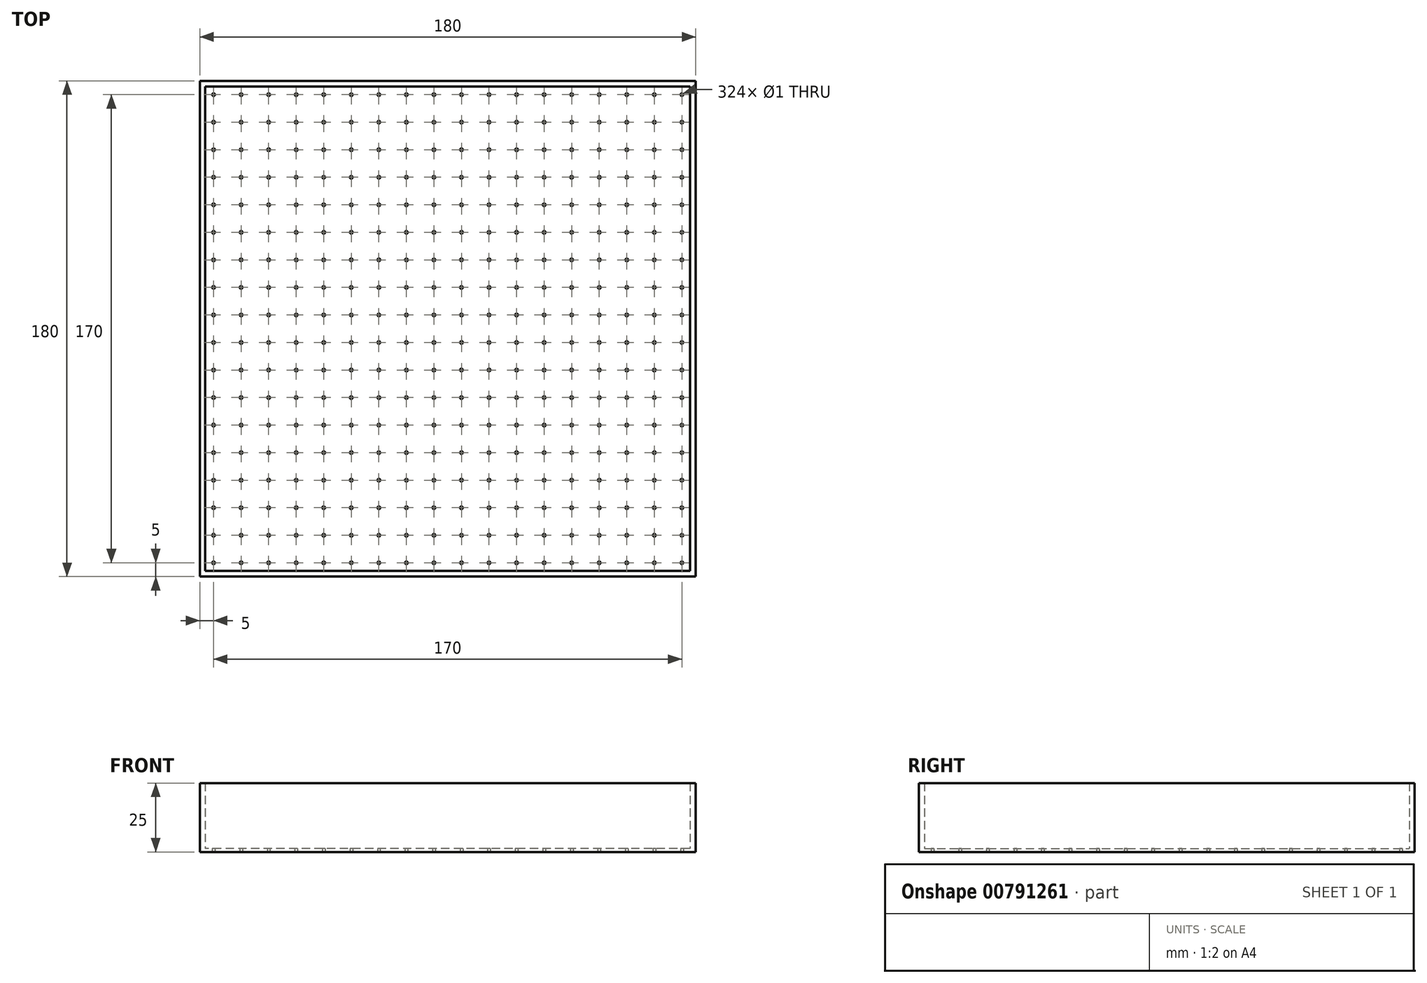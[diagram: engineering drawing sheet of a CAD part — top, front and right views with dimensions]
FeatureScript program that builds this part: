
annotation { "Feature Type Name" : "Feature", "Feature Type Description" : "" }
export const myFeature = defineFeature(function(context is Context, id is Id, definition is map)
    precondition{}
    {
        {
            var Q0;
            Q0=qCreatedBy(makeId("Top.planeOp"),FACE);
            var sketch = newSketch(context, id + "F0", { "sketchPlane" : qUnion([Q0])});
            skLineSegment(sketch, "E0.bottom", {"start": v(0, 0) * mm, "end": v(180, 0) * mm});
            skLineSegment(sketch, "E0.top", {"start": v(0, -180) * mm, "end": v(180, -180) * mm});
            skLineSegment(sketch, "E0.left", {"start": v(0, 0) * mm, "end": v(0, -180) * mm});
            skLineSegment(sketch, "E0.right", {"start": v(180, 0) * mm, "end": v(180, -180) * mm});
            skLineSegment(sketch, "E1.bottom", {"start": v(2, -2) * mm, "end": v(178, -2) * mm});
            skLineSegment(sketch, "E1.top", {"start": v(2, -178) * mm, "end": v(178, -178) * mm});
            skLineSegment(sketch, "E1.left", {"start": v(2, -2) * mm, "end": v(2, -178) * mm});
            skLineSegment(sketch, "E1.right", {"start": v(178, -2) * mm, "end": v(178, -178) * mm});
            skCircle(sketch, "E2", {"center": v(5, -5) * mm, "radius": 0.5 * mm});
            skCircle(sketch, "E3.1.0.0", {"center": v(15, -5) * mm, "radius": 0.5 * mm});
            skCircle(sketch, "E3.2.0.0", {"center": v(25, -5) * mm, "radius": 0.5 * mm});
            skLineSegment(sketch, "E3.direction1", {"start": v(5, -5) * mm, "end": v(15, -5) * mm, "construction": true});
            skCircle(sketch, "E4.0.3.0", {"center": v(35, -5) * mm, "radius": 0.5 * mm});
            skCircle(sketch, "E4.0.4.0", {"center": v(45, -5) * mm, "radius": 0.5 * mm});
            skCircle(sketch, "E4.0.5.0", {"center": v(55, -5) * mm, "radius": 0.5 * mm});
            skCircle(sketch, "E4.0.6.0", {"center": v(65, -5) * mm, "radius": 0.5 * mm});
            skCircle(sketch, "E4.0.7.0", {"center": v(75, -5) * mm, "radius": 0.5 * mm});
            skCircle(sketch, "E4.0.8.0", {"center": v(85, -5) * mm, "radius": 0.5 * mm});
            skCircle(sketch, "E4.0.9.0", {"center": v(95, -5) * mm, "radius": 0.5 * mm});
            skCircle(sketch, "E4.0.10.0", {"center": v(105, -5) * mm, "radius": 0.5 * mm});
            skCircle(sketch, "E4.0.11.0", {"center": v(115, -5) * mm, "radius": 0.5 * mm});
            skCircle(sketch, "E4.0.12.0", {"center": v(125, -5) * mm, "radius": 0.5 * mm});
            skCircle(sketch, "E4.0.13.0", {"center": v(135, -5) * mm, "radius": 0.5 * mm});
            skCircle(sketch, "E4.0.14.0", {"center": v(145, -5) * mm, "radius": 0.5 * mm});
            skCircle(sketch, "E4.0.15.0", {"center": v(155, -5) * mm, "radius": 0.5 * mm});
            skCircle(sketch, "E4.0.16.0", {"center": v(165, -5) * mm, "radius": 0.5 * mm});
            skCircle(sketch, "E4.0.17.0", {"center": v(175, -5) * mm, "radius": 0.5 * mm});
            skLineSegment(sketch, "E5.1.0.0", {"start": v(5, -15) * mm, "end": v(15, -15) * mm, "construction": true});
            skCircle(sketch, "E5.1.0.1", {"center": v(125, -15) * mm, "radius": 0.5 * mm});
            skCircle(sketch, "E5.1.0.2", {"center": v(115, -15) * mm, "radius": 0.5 * mm});
            skCircle(sketch, "E5.1.0.3", {"center": v(105, -15) * mm, "radius": 0.5 * mm});
            skCircle(sketch, "E5.1.0.4", {"center": v(65, -15) * mm, "radius": 0.5 * mm});
            skCircle(sketch, "E5.1.0.5", {"center": v(135, -15) * mm, "radius": 0.5 * mm});
            skCircle(sketch, "E5.1.0.6", {"center": v(45, -15) * mm, "radius": 0.5 * mm});
            skCircle(sketch, "E5.1.0.7", {"center": v(85, -15) * mm, "radius": 0.5 * mm});
            skCircle(sketch, "E5.1.0.8", {"center": v(95, -15) * mm, "radius": 0.5 * mm});
            skCircle(sketch, "E5.1.0.9", {"center": v(75, -15) * mm, "radius": 0.5 * mm});
            skCircle(sketch, "E5.1.0.10", {"center": v(55, -15) * mm, "radius": 0.5 * mm});
            skCircle(sketch, "E5.1.0.11", {"center": v(25, -15) * mm, "radius": 0.5 * mm});
            skCircle(sketch, "E5.1.0.12", {"center": v(35, -15) * mm, "radius": 0.5 * mm});
            skCircle(sketch, "E5.1.0.13", {"center": v(15, -15) * mm, "radius": 0.5 * mm});
            skCircle(sketch, "E5.1.0.14", {"center": v(5, -15) * mm, "radius": 0.5 * mm});
            skCircle(sketch, "E5.1.0.15", {"center": v(175, -15) * mm, "radius": 0.5 * mm});
            skCircle(sketch, "E5.1.0.16", {"center": v(155, -15) * mm, "radius": 0.5 * mm});
            skCircle(sketch, "E5.1.0.17", {"center": v(145, -15) * mm, "radius": 0.5 * mm});
            skCircle(sketch, "E5.1.0.18", {"center": v(165, -15) * mm, "radius": 0.5 * mm});
            skLineSegment(sketch, "E5.2.0.0", {"start": v(5, -25) * mm, "end": v(15, -25) * mm, "construction": true});
            skCircle(sketch, "E5.2.0.1", {"center": v(125, -25) * mm, "radius": 0.5 * mm});
            skCircle(sketch, "E5.2.0.2", {"center": v(115, -25) * mm, "radius": 0.5 * mm});
            skCircle(sketch, "E5.2.0.3", {"center": v(105, -25) * mm, "radius": 0.5 * mm});
            skCircle(sketch, "E5.2.0.4", {"center": v(65, -25) * mm, "radius": 0.5 * mm});
            skCircle(sketch, "E5.2.0.5", {"center": v(135, -25) * mm, "radius": 0.5 * mm});
            skCircle(sketch, "E5.2.0.6", {"center": v(45, -25) * mm, "radius": 0.5 * mm});
            skCircle(sketch, "E5.2.0.7", {"center": v(85, -25) * mm, "radius": 0.5 * mm});
            skCircle(sketch, "E5.2.0.8", {"center": v(95, -25) * mm, "radius": 0.5 * mm});
            skCircle(sketch, "E5.2.0.9", {"center": v(75, -25) * mm, "radius": 0.5 * mm});
            skCircle(sketch, "E5.2.0.10", {"center": v(55, -25) * mm, "radius": 0.5 * mm});
            skCircle(sketch, "E5.2.0.11", {"center": v(25, -25) * mm, "radius": 0.5 * mm});
            skCircle(sketch, "E5.2.0.12", {"center": v(35, -25) * mm, "radius": 0.5 * mm});
            skCircle(sketch, "E5.2.0.13", {"center": v(15, -25) * mm, "radius": 0.5 * mm});
            skCircle(sketch, "E5.2.0.14", {"center": v(5, -25) * mm, "radius": 0.5 * mm});
            skCircle(sketch, "E5.2.0.15", {"center": v(175, -25) * mm, "radius": 0.5 * mm});
            skCircle(sketch, "E5.2.0.16", {"center": v(155, -25) * mm, "radius": 0.5 * mm});
            skCircle(sketch, "E5.2.0.17", {"center": v(145, -25) * mm, "radius": 0.5 * mm});
            skCircle(sketch, "E5.2.0.18", {"center": v(165, -25) * mm, "radius": 0.5 * mm});
            skLineSegment(sketch, "E5.3.0.0", {"start": v(5, -35) * mm, "end": v(15, -35) * mm, "construction": true});
            skCircle(sketch, "E5.3.0.1", {"center": v(125, -35) * mm, "radius": 0.5 * mm});
            skCircle(sketch, "E5.3.0.2", {"center": v(115, -35) * mm, "radius": 0.5 * mm});
            skCircle(sketch, "E5.3.0.3", {"center": v(105, -35) * mm, "radius": 0.5 * mm});
            skCircle(sketch, "E5.3.0.4", {"center": v(65, -35) * mm, "radius": 0.5 * mm});
            skCircle(sketch, "E5.3.0.5", {"center": v(135, -35) * mm, "radius": 0.5 * mm});
            skCircle(sketch, "E5.3.0.6", {"center": v(45, -35) * mm, "radius": 0.5 * mm});
            skCircle(sketch, "E5.3.0.7", {"center": v(85, -35) * mm, "radius": 0.5 * mm});
            skCircle(sketch, "E5.3.0.8", {"center": v(95, -35) * mm, "radius": 0.5 * mm});
            skCircle(sketch, "E5.3.0.9", {"center": v(75, -35) * mm, "radius": 0.5 * mm});
            skCircle(sketch, "E5.3.0.10", {"center": v(55, -35) * mm, "radius": 0.5 * mm});
            skCircle(sketch, "E5.3.0.11", {"center": v(25, -35) * mm, "radius": 0.5 * mm});
            skCircle(sketch, "E5.3.0.12", {"center": v(35, -35) * mm, "radius": 0.5 * mm});
            skCircle(sketch, "E5.3.0.13", {"center": v(15, -35) * mm, "radius": 0.5 * mm});
            skCircle(sketch, "E5.3.0.14", {"center": v(5, -35) * mm, "radius": 0.5 * mm});
            skCircle(sketch, "E5.3.0.15", {"center": v(175, -35) * mm, "radius": 0.5 * mm});
            skCircle(sketch, "E5.3.0.16", {"center": v(155, -35) * mm, "radius": 0.5 * mm});
            skCircle(sketch, "E5.3.0.17", {"center": v(145, -35) * mm, "radius": 0.5 * mm});
            skCircle(sketch, "E5.3.0.18", {"center": v(165, -35) * mm, "radius": 0.5 * mm});
            skLineSegment(sketch, "E5.4.0.0", {"start": v(5, -45) * mm, "end": v(15, -45) * mm, "construction": true});
            skCircle(sketch, "E5.4.0.1", {"center": v(125, -45) * mm, "radius": 0.5 * mm});
            skCircle(sketch, "E5.4.0.2", {"center": v(115, -45) * mm, "radius": 0.5 * mm});
            skCircle(sketch, "E5.4.0.3", {"center": v(105, -45) * mm, "radius": 0.5 * mm});
            skCircle(sketch, "E5.4.0.4", {"center": v(65, -45) * mm, "radius": 0.5 * mm});
            skCircle(sketch, "E5.4.0.5", {"center": v(135, -45) * mm, "radius": 0.5 * mm});
            skCircle(sketch, "E5.4.0.6", {"center": v(45, -45) * mm, "radius": 0.5 * mm});
            skCircle(sketch, "E5.4.0.7", {"center": v(85, -45) * mm, "radius": 0.5 * mm});
            skCircle(sketch, "E5.4.0.8", {"center": v(95, -45) * mm, "radius": 0.5 * mm});
            skCircle(sketch, "E5.4.0.9", {"center": v(75, -45) * mm, "radius": 0.5 * mm});
            skCircle(sketch, "E5.4.0.10", {"center": v(55, -45) * mm, "radius": 0.5 * mm});
            skCircle(sketch, "E5.4.0.11", {"center": v(25, -45) * mm, "radius": 0.5 * mm});
            skCircle(sketch, "E5.4.0.12", {"center": v(35, -45) * mm, "radius": 0.5 * mm});
            skCircle(sketch, "E5.4.0.13", {"center": v(15, -45) * mm, "radius": 0.5 * mm});
            skCircle(sketch, "E5.4.0.14", {"center": v(5, -45) * mm, "radius": 0.5 * mm});
            skCircle(sketch, "E5.4.0.15", {"center": v(175, -45) * mm, "radius": 0.5 * mm});
            skCircle(sketch, "E5.4.0.16", {"center": v(155, -45) * mm, "radius": 0.5 * mm});
            skCircle(sketch, "E5.4.0.17", {"center": v(145, -45) * mm, "radius": 0.5 * mm});
            skCircle(sketch, "E5.4.0.18", {"center": v(165, -45) * mm, "radius": 0.5 * mm});
            skLineSegment(sketch, "E5.5.0.0", {"start": v(5, -55) * mm, "end": v(15, -55) * mm, "construction": true});
            skCircle(sketch, "E5.5.0.1", {"center": v(125, -55) * mm, "radius": 0.5 * mm});
            skCircle(sketch, "E5.5.0.2", {"center": v(115, -55) * mm, "radius": 0.5 * mm});
            skCircle(sketch, "E5.5.0.3", {"center": v(105, -55) * mm, "radius": 0.5 * mm});
            skCircle(sketch, "E5.5.0.4", {"center": v(65, -55) * mm, "radius": 0.5 * mm});
            skCircle(sketch, "E5.5.0.5", {"center": v(135, -55) * mm, "radius": 0.5 * mm});
            skCircle(sketch, "E5.5.0.6", {"center": v(45, -55) * mm, "radius": 0.5 * mm});
            skCircle(sketch, "E5.5.0.7", {"center": v(85, -55) * mm, "radius": 0.5 * mm});
            skCircle(sketch, "E5.5.0.8", {"center": v(95, -55) * mm, "radius": 0.5 * mm});
            skCircle(sketch, "E5.5.0.9", {"center": v(75, -55) * mm, "radius": 0.5 * mm});
            skCircle(sketch, "E5.5.0.10", {"center": v(55, -55) * mm, "radius": 0.5 * mm});
            skCircle(sketch, "E5.5.0.11", {"center": v(25, -55) * mm, "radius": 0.5 * mm});
            skCircle(sketch, "E5.5.0.12", {"center": v(35, -55) * mm, "radius": 0.5 * mm});
            skCircle(sketch, "E5.5.0.13", {"center": v(15, -55) * mm, "radius": 0.5 * mm});
            skCircle(sketch, "E5.5.0.14", {"center": v(5, -55) * mm, "radius": 0.5 * mm});
            skCircle(sketch, "E5.5.0.15", {"center": v(175, -55) * mm, "radius": 0.5 * mm});
            skCircle(sketch, "E5.5.0.16", {"center": v(155, -55) * mm, "radius": 0.5 * mm});
            skCircle(sketch, "E5.5.0.17", {"center": v(145, -55) * mm, "radius": 0.5 * mm});
            skCircle(sketch, "E5.5.0.18", {"center": v(165, -55) * mm, "radius": 0.5 * mm});
            skLineSegment(sketch, "E5.6.0.0", {"start": v(5, -65) * mm, "end": v(15, -65) * mm, "construction": true});
            skCircle(sketch, "E5.6.0.1", {"center": v(125, -65) * mm, "radius": 0.5 * mm});
            skCircle(sketch, "E5.6.0.2", {"center": v(115, -65) * mm, "radius": 0.5 * mm});
            skCircle(sketch, "E5.6.0.3", {"center": v(105, -65) * mm, "radius": 0.5 * mm});
            skCircle(sketch, "E5.6.0.4", {"center": v(65, -65) * mm, "radius": 0.5 * mm});
            skCircle(sketch, "E5.6.0.5", {"center": v(135, -65) * mm, "radius": 0.5 * mm});
            skCircle(sketch, "E5.6.0.6", {"center": v(45, -65) * mm, "radius": 0.5 * mm});
            skCircle(sketch, "E5.6.0.7", {"center": v(85, -65) * mm, "radius": 0.5 * mm});
            skCircle(sketch, "E5.6.0.8", {"center": v(95, -65) * mm, "radius": 0.5 * mm});
            skCircle(sketch, "E5.6.0.9", {"center": v(75, -65) * mm, "radius": 0.5 * mm});
            skCircle(sketch, "E5.6.0.10", {"center": v(55, -65) * mm, "radius": 0.5 * mm});
            skCircle(sketch, "E5.6.0.11", {"center": v(25, -65) * mm, "radius": 0.5 * mm});
            skCircle(sketch, "E5.6.0.12", {"center": v(35, -65) * mm, "radius": 0.5 * mm});
            skCircle(sketch, "E5.6.0.13", {"center": v(15, -65) * mm, "radius": 0.5 * mm});
            skCircle(sketch, "E5.6.0.14", {"center": v(5, -65) * mm, "radius": 0.5 * mm});
            skCircle(sketch, "E5.6.0.15", {"center": v(175, -65) * mm, "radius": 0.5 * mm});
            skCircle(sketch, "E5.6.0.16", {"center": v(155, -65) * mm, "radius": 0.5 * mm});
            skCircle(sketch, "E5.6.0.17", {"center": v(145, -65) * mm, "radius": 0.5 * mm});
            skCircle(sketch, "E5.6.0.18", {"center": v(165, -65) * mm, "radius": 0.5 * mm});
            skLineSegment(sketch, "E5.7.0.0", {"start": v(5, -75) * mm, "end": v(15, -75) * mm, "construction": true});
            skCircle(sketch, "E5.7.0.1", {"center": v(125, -75) * mm, "radius": 0.5 * mm});
            skCircle(sketch, "E5.7.0.2", {"center": v(115, -75) * mm, "radius": 0.5 * mm});
            skCircle(sketch, "E5.7.0.3", {"center": v(105, -75) * mm, "radius": 0.5 * mm});
            skCircle(sketch, "E5.7.0.4", {"center": v(65, -75) * mm, "radius": 0.5 * mm});
            skCircle(sketch, "E5.7.0.5", {"center": v(135, -75) * mm, "radius": 0.5 * mm});
            skCircle(sketch, "E5.7.0.6", {"center": v(45, -75) * mm, "radius": 0.5 * mm});
            skCircle(sketch, "E5.7.0.7", {"center": v(85, -75) * mm, "radius": 0.5 * mm});
            skCircle(sketch, "E5.7.0.8", {"center": v(95, -75) * mm, "radius": 0.5 * mm});
            skCircle(sketch, "E5.7.0.9", {"center": v(75, -75) * mm, "radius": 0.5 * mm});
            skCircle(sketch, "E5.7.0.10", {"center": v(55, -75) * mm, "radius": 0.5 * mm});
            skCircle(sketch, "E5.7.0.11", {"center": v(25, -75) * mm, "radius": 0.5 * mm});
            skCircle(sketch, "E5.7.0.12", {"center": v(35, -75) * mm, "radius": 0.5 * mm});
            skCircle(sketch, "E5.7.0.13", {"center": v(15, -75) * mm, "radius": 0.5 * mm});
            skCircle(sketch, "E5.7.0.14", {"center": v(5, -75) * mm, "radius": 0.5 * mm});
            skCircle(sketch, "E5.7.0.15", {"center": v(175, -75) * mm, "radius": 0.5 * mm});
            skCircle(sketch, "E5.7.0.16", {"center": v(155, -75) * mm, "radius": 0.5 * mm});
            skCircle(sketch, "E5.7.0.17", {"center": v(145, -75) * mm, "radius": 0.5 * mm});
            skCircle(sketch, "E5.7.0.18", {"center": v(165, -75) * mm, "radius": 0.5 * mm});
            skLineSegment(sketch, "E5.8.0.0", {"start": v(5, -85) * mm, "end": v(15, -85) * mm, "construction": true});
            skCircle(sketch, "E5.8.0.1", {"center": v(125, -85) * mm, "radius": 0.5 * mm});
            skCircle(sketch, "E5.8.0.2", {"center": v(115, -85) * mm, "radius": 0.5 * mm});
            skCircle(sketch, "E5.8.0.3", {"center": v(105, -85) * mm, "radius": 0.5 * mm});
            skCircle(sketch, "E5.8.0.4", {"center": v(65, -85) * mm, "radius": 0.5 * mm});
            skCircle(sketch, "E5.8.0.5", {"center": v(135, -85) * mm, "radius": 0.5 * mm});
            skCircle(sketch, "E5.8.0.6", {"center": v(45, -85) * mm, "radius": 0.5 * mm});
            skCircle(sketch, "E5.8.0.7", {"center": v(85, -85) * mm, "radius": 0.5 * mm});
            skCircle(sketch, "E5.8.0.8", {"center": v(95, -85) * mm, "radius": 0.5 * mm});
            skCircle(sketch, "E5.8.0.9", {"center": v(75, -85) * mm, "radius": 0.5 * mm});
            skCircle(sketch, "E5.8.0.10", {"center": v(55, -85) * mm, "radius": 0.5 * mm});
            skCircle(sketch, "E5.8.0.11", {"center": v(25, -85) * mm, "radius": 0.5 * mm});
            skCircle(sketch, "E5.8.0.12", {"center": v(35, -85) * mm, "radius": 0.5 * mm});
            skCircle(sketch, "E5.8.0.13", {"center": v(15, -85) * mm, "radius": 0.5 * mm});
            skCircle(sketch, "E5.8.0.14", {"center": v(5, -85) * mm, "radius": 0.5 * mm});
            skCircle(sketch, "E5.8.0.15", {"center": v(175, -85) * mm, "radius": 0.5 * mm});
            skCircle(sketch, "E5.8.0.16", {"center": v(155, -85) * mm, "radius": 0.5 * mm});
            skCircle(sketch, "E5.8.0.17", {"center": v(145, -85) * mm, "radius": 0.5 * mm});
            skCircle(sketch, "E5.8.0.18", {"center": v(165, -85) * mm, "radius": 0.5 * mm});
            skLineSegment(sketch, "E5.9.0.0", {"start": v(5, -95) * mm, "end": v(15, -95) * mm, "construction": true});
            skCircle(sketch, "E5.9.0.1", {"center": v(125, -95) * mm, "radius": 0.5 * mm});
            skCircle(sketch, "E5.9.0.2", {"center": v(115, -95) * mm, "radius": 0.5 * mm});
            skCircle(sketch, "E5.9.0.3", {"center": v(105, -95) * mm, "radius": 0.5 * mm});
            skCircle(sketch, "E5.9.0.4", {"center": v(65, -95) * mm, "radius": 0.5 * mm});
            skCircle(sketch, "E5.9.0.5", {"center": v(135, -95) * mm, "radius": 0.5 * mm});
            skCircle(sketch, "E5.9.0.6", {"center": v(45, -95) * mm, "radius": 0.5 * mm});
            skCircle(sketch, "E5.9.0.7", {"center": v(85, -95) * mm, "radius": 0.5 * mm});
            skCircle(sketch, "E5.9.0.8", {"center": v(95, -95) * mm, "radius": 0.5 * mm});
            skCircle(sketch, "E5.9.0.9", {"center": v(75, -95) * mm, "radius": 0.5 * mm});
            skCircle(sketch, "E5.9.0.10", {"center": v(55, -95) * mm, "radius": 0.5 * mm});
            skCircle(sketch, "E5.9.0.11", {"center": v(25, -95) * mm, "radius": 0.5 * mm});
            skCircle(sketch, "E5.9.0.12", {"center": v(35, -95) * mm, "radius": 0.5 * mm});
            skCircle(sketch, "E5.9.0.13", {"center": v(15, -95) * mm, "radius": 0.5 * mm});
            skCircle(sketch, "E5.9.0.14", {"center": v(5, -95) * mm, "radius": 0.5 * mm});
            skCircle(sketch, "E5.9.0.15", {"center": v(175, -95) * mm, "radius": 0.5 * mm});
            skCircle(sketch, "E5.9.0.16", {"center": v(155, -95) * mm, "radius": 0.5 * mm});
            skCircle(sketch, "E5.9.0.17", {"center": v(145, -95) * mm, "radius": 0.5 * mm});
            skCircle(sketch, "E5.9.0.18", {"center": v(165, -95) * mm, "radius": 0.5 * mm});
            skLineSegment(sketch, "E5.10.0.0", {"start": v(5, -105) * mm, "end": v(15, -105) * mm, "construction": true});
            skCircle(sketch, "E5.10.0.1", {"center": v(125, -105) * mm, "radius": 0.5 * mm});
            skCircle(sketch, "E5.10.0.2", {"center": v(115, -105) * mm, "radius": 0.5 * mm});
            skCircle(sketch, "E5.10.0.3", {"center": v(105, -105) * mm, "radius": 0.5 * mm});
            skCircle(sketch, "E5.10.0.4", {"center": v(65, -105) * mm, "radius": 0.5 * mm});
            skCircle(sketch, "E5.10.0.5", {"center": v(135, -105) * mm, "radius": 0.5 * mm});
            skCircle(sketch, "E5.10.0.6", {"center": v(45, -105) * mm, "radius": 0.5 * mm});
            skCircle(sketch, "E5.10.0.7", {"center": v(85, -105) * mm, "radius": 0.5 * mm});
            skCircle(sketch, "E5.10.0.8", {"center": v(95, -105) * mm, "radius": 0.5 * mm});
            skCircle(sketch, "E5.10.0.9", {"center": v(75, -105) * mm, "radius": 0.5 * mm});
            skCircle(sketch, "E5.10.0.10", {"center": v(55, -105) * mm, "radius": 0.5 * mm});
            skCircle(sketch, "E5.10.0.11", {"center": v(25, -105) * mm, "radius": 0.5 * mm});
            skCircle(sketch, "E5.10.0.12", {"center": v(35, -105) * mm, "radius": 0.5 * mm});
            skCircle(sketch, "E5.10.0.13", {"center": v(15, -105) * mm, "radius": 0.5 * mm});
            skCircle(sketch, "E5.10.0.14", {"center": v(5, -105) * mm, "radius": 0.5 * mm});
            skCircle(sketch, "E5.10.0.15", {"center": v(175, -105) * mm, "radius": 0.5 * mm});
            skCircle(sketch, "E5.10.0.16", {"center": v(155, -105) * mm, "radius": 0.5 * mm});
            skCircle(sketch, "E5.10.0.17", {"center": v(145, -105) * mm, "radius": 0.5 * mm});
            skCircle(sketch, "E5.10.0.18", {"center": v(165, -105) * mm, "radius": 0.5 * mm});
            skLineSegment(sketch, "E5.11.0.0", {"start": v(5, -115) * mm, "end": v(15, -115) * mm, "construction": true});
            skCircle(sketch, "E5.11.0.1", {"center": v(125, -115) * mm, "radius": 0.5 * mm});
            skCircle(sketch, "E5.11.0.2", {"center": v(115, -115) * mm, "radius": 0.5 * mm});
            skCircle(sketch, "E5.11.0.3", {"center": v(105, -115) * mm, "radius": 0.5 * mm});
            skCircle(sketch, "E5.11.0.4", {"center": v(65, -115) * mm, "radius": 0.5 * mm});
            skCircle(sketch, "E5.11.0.5", {"center": v(135, -115) * mm, "radius": 0.5 * mm});
            skCircle(sketch, "E5.11.0.6", {"center": v(45, -115) * mm, "radius": 0.5 * mm});
            skCircle(sketch, "E5.11.0.7", {"center": v(85, -115) * mm, "radius": 0.5 * mm});
            skCircle(sketch, "E5.11.0.8", {"center": v(95, -115) * mm, "radius": 0.5 * mm});
            skCircle(sketch, "E5.11.0.9", {"center": v(75, -115) * mm, "radius": 0.5 * mm});
            skCircle(sketch, "E5.11.0.10", {"center": v(55, -115) * mm, "radius": 0.5 * mm});
            skCircle(sketch, "E5.11.0.11", {"center": v(25, -115) * mm, "radius": 0.5 * mm});
            skCircle(sketch, "E5.11.0.12", {"center": v(35, -115) * mm, "radius": 0.5 * mm});
            skCircle(sketch, "E5.11.0.13", {"center": v(15, -115) * mm, "radius": 0.5 * mm});
            skCircle(sketch, "E5.11.0.14", {"center": v(5, -115) * mm, "radius": 0.5 * mm});
            skCircle(sketch, "E5.11.0.15", {"center": v(175, -115) * mm, "radius": 0.5 * mm});
            skCircle(sketch, "E5.11.0.16", {"center": v(155, -115) * mm, "radius": 0.5 * mm});
            skCircle(sketch, "E5.11.0.17", {"center": v(145, -115) * mm, "radius": 0.5 * mm});
            skCircle(sketch, "E5.11.0.18", {"center": v(165, -115) * mm, "radius": 0.5 * mm});
            skLineSegment(sketch, "E5.12.0.0", {"start": v(5, -125) * mm, "end": v(15, -125) * mm, "construction": true});
            skCircle(sketch, "E5.12.0.1", {"center": v(125, -125) * mm, "radius": 0.5 * mm});
            skCircle(sketch, "E5.12.0.2", {"center": v(115, -125) * mm, "radius": 0.5 * mm});
            skCircle(sketch, "E5.12.0.3", {"center": v(105, -125) * mm, "radius": 0.5 * mm});
            skCircle(sketch, "E5.12.0.4", {"center": v(65, -125) * mm, "radius": 0.5 * mm});
            skCircle(sketch, "E5.12.0.5", {"center": v(135, -125) * mm, "radius": 0.5 * mm});
            skCircle(sketch, "E5.12.0.6", {"center": v(45, -125) * mm, "radius": 0.5 * mm});
            skCircle(sketch, "E5.12.0.7", {"center": v(85, -125) * mm, "radius": 0.5 * mm});
            skCircle(sketch, "E5.12.0.8", {"center": v(95, -125) * mm, "radius": 0.5 * mm});
            skCircle(sketch, "E5.12.0.9", {"center": v(75, -125) * mm, "radius": 0.5 * mm});
            skCircle(sketch, "E5.12.0.10", {"center": v(55, -125) * mm, "radius": 0.5 * mm});
            skCircle(sketch, "E5.12.0.11", {"center": v(25, -125) * mm, "radius": 0.5 * mm});
            skCircle(sketch, "E5.12.0.12", {"center": v(35, -125) * mm, "radius": 0.5 * mm});
            skCircle(sketch, "E5.12.0.13", {"center": v(15, -125) * mm, "radius": 0.5 * mm});
            skCircle(sketch, "E5.12.0.14", {"center": v(5, -125) * mm, "radius": 0.5 * mm});
            skCircle(sketch, "E5.12.0.15", {"center": v(175, -125) * mm, "radius": 0.5 * mm});
            skCircle(sketch, "E5.12.0.16", {"center": v(155, -125) * mm, "radius": 0.5 * mm});
            skCircle(sketch, "E5.12.0.17", {"center": v(145, -125) * mm, "radius": 0.5 * mm});
            skCircle(sketch, "E5.12.0.18", {"center": v(165, -125) * mm, "radius": 0.5 * mm});
            skLineSegment(sketch, "E5.13.0.0", {"start": v(5, -135) * mm, "end": v(15, -135) * mm, "construction": true});
            skCircle(sketch, "E5.13.0.1", {"center": v(125, -135) * mm, "radius": 0.5 * mm});
            skCircle(sketch, "E5.13.0.2", {"center": v(115, -135) * mm, "radius": 0.5 * mm});
            skCircle(sketch, "E5.13.0.3", {"center": v(105, -135) * mm, "radius": 0.5 * mm});
            skCircle(sketch, "E5.13.0.4", {"center": v(65, -135) * mm, "radius": 0.5 * mm});
            skCircle(sketch, "E5.13.0.5", {"center": v(135, -135) * mm, "radius": 0.5 * mm});
            skCircle(sketch, "E5.13.0.6", {"center": v(45, -135) * mm, "radius": 0.5 * mm});
            skCircle(sketch, "E5.13.0.7", {"center": v(85, -135) * mm, "radius": 0.5 * mm});
            skCircle(sketch, "E5.13.0.8", {"center": v(95, -135) * mm, "radius": 0.5 * mm});
            skCircle(sketch, "E5.13.0.9", {"center": v(75, -135) * mm, "radius": 0.5 * mm});
            skCircle(sketch, "E5.13.0.10", {"center": v(55, -135) * mm, "radius": 0.5 * mm});
            skCircle(sketch, "E5.13.0.11", {"center": v(25, -135) * mm, "radius": 0.5 * mm});
            skCircle(sketch, "E5.13.0.12", {"center": v(35, -135) * mm, "radius": 0.5 * mm});
            skCircle(sketch, "E5.13.0.13", {"center": v(15, -135) * mm, "radius": 0.5 * mm});
            skCircle(sketch, "E5.13.0.14", {"center": v(5, -135) * mm, "radius": 0.5 * mm});
            skCircle(sketch, "E5.13.0.15", {"center": v(175, -135) * mm, "radius": 0.5 * mm});
            skCircle(sketch, "E5.13.0.16", {"center": v(155, -135) * mm, "radius": 0.5 * mm});
            skCircle(sketch, "E5.13.0.17", {"center": v(145, -135) * mm, "radius": 0.5 * mm});
            skCircle(sketch, "E5.13.0.18", {"center": v(165, -135) * mm, "radius": 0.5 * mm});
            skLineSegment(sketch, "E5.14.0.0", {"start": v(5, -145) * mm, "end": v(15, -145) * mm, "construction": true});
            skCircle(sketch, "E5.14.0.1", {"center": v(125, -145) * mm, "radius": 0.5 * mm});
            skCircle(sketch, "E5.14.0.2", {"center": v(115, -145) * mm, "radius": 0.5 * mm});
            skCircle(sketch, "E5.14.0.3", {"center": v(105, -145) * mm, "radius": 0.5 * mm});
            skCircle(sketch, "E5.14.0.4", {"center": v(65, -145) * mm, "radius": 0.5 * mm});
            skCircle(sketch, "E5.14.0.5", {"center": v(135, -145) * mm, "radius": 0.5 * mm});
            skCircle(sketch, "E5.14.0.6", {"center": v(45, -145) * mm, "radius": 0.5 * mm});
            skCircle(sketch, "E5.14.0.7", {"center": v(85, -145) * mm, "radius": 0.5 * mm});
            skCircle(sketch, "E5.14.0.8", {"center": v(95, -145) * mm, "radius": 0.5 * mm});
            skCircle(sketch, "E5.14.0.9", {"center": v(75, -145) * mm, "radius": 0.5 * mm});
            skCircle(sketch, "E5.14.0.10", {"center": v(55, -145) * mm, "radius": 0.5 * mm});
            skCircle(sketch, "E5.14.0.11", {"center": v(25, -145) * mm, "radius": 0.5 * mm});
            skCircle(sketch, "E5.14.0.12", {"center": v(35, -145) * mm, "radius": 0.5 * mm});
            skCircle(sketch, "E5.14.0.13", {"center": v(15, -145) * mm, "radius": 0.5 * mm});
            skCircle(sketch, "E5.14.0.14", {"center": v(5, -145) * mm, "radius": 0.5 * mm});
            skCircle(sketch, "E5.14.0.15", {"center": v(175, -145) * mm, "radius": 0.5 * mm});
            skCircle(sketch, "E5.14.0.16", {"center": v(155, -145) * mm, "radius": 0.5 * mm});
            skCircle(sketch, "E5.14.0.17", {"center": v(145, -145) * mm, "radius": 0.5 * mm});
            skCircle(sketch, "E5.14.0.18", {"center": v(165, -145) * mm, "radius": 0.5 * mm});
            skLineSegment(sketch, "E5.15.0.0", {"start": v(5, -155) * mm, "end": v(15, -155) * mm, "construction": true});
            skCircle(sketch, "E5.15.0.1", {"center": v(125, -155) * mm, "radius": 0.5 * mm});
            skCircle(sketch, "E5.15.0.2", {"center": v(115, -155) * mm, "radius": 0.5 * mm});
            skCircle(sketch, "E5.15.0.3", {"center": v(105, -155) * mm, "radius": 0.5 * mm});
            skCircle(sketch, "E5.15.0.4", {"center": v(65, -155) * mm, "radius": 0.5 * mm});
            skCircle(sketch, "E5.15.0.5", {"center": v(135, -155) * mm, "radius": 0.5 * mm});
            skCircle(sketch, "E5.15.0.6", {"center": v(45, -155) * mm, "radius": 0.5 * mm});
            skCircle(sketch, "E5.15.0.7", {"center": v(85, -155) * mm, "radius": 0.5 * mm});
            skCircle(sketch, "E5.15.0.8", {"center": v(95, -155) * mm, "radius": 0.5 * mm});
            skCircle(sketch, "E5.15.0.9", {"center": v(75, -155) * mm, "radius": 0.5 * mm});
            skCircle(sketch, "E5.15.0.10", {"center": v(55, -155) * mm, "radius": 0.5 * mm});
            skCircle(sketch, "E5.15.0.11", {"center": v(25, -155) * mm, "radius": 0.5 * mm});
            skCircle(sketch, "E5.15.0.12", {"center": v(35, -155) * mm, "radius": 0.5 * mm});
            skCircle(sketch, "E5.15.0.13", {"center": v(15, -155) * mm, "radius": 0.5 * mm});
            skCircle(sketch, "E5.15.0.14", {"center": v(5, -155) * mm, "radius": 0.5 * mm});
            skCircle(sketch, "E5.15.0.15", {"center": v(175, -155) * mm, "radius": 0.5 * mm});
            skCircle(sketch, "E5.15.0.16", {"center": v(155, -155) * mm, "radius": 0.5 * mm});
            skCircle(sketch, "E5.15.0.17", {"center": v(145, -155) * mm, "radius": 0.5 * mm});
            skCircle(sketch, "E5.15.0.18", {"center": v(165, -155) * mm, "radius": 0.5 * mm});
            skLineSegment(sketch, "E5.16.0.0", {"start": v(5, -165) * mm, "end": v(15, -165) * mm, "construction": true});
            skCircle(sketch, "E5.16.0.1", {"center": v(125, -165) * mm, "radius": 0.5 * mm});
            skCircle(sketch, "E5.16.0.2", {"center": v(115, -165) * mm, "radius": 0.5 * mm});
            skCircle(sketch, "E5.16.0.3", {"center": v(105, -165) * mm, "radius": 0.5 * mm});
            skCircle(sketch, "E5.16.0.4", {"center": v(65, -165) * mm, "radius": 0.5 * mm});
            skCircle(sketch, "E5.16.0.5", {"center": v(135, -165) * mm, "radius": 0.5 * mm});
            skCircle(sketch, "E5.16.0.6", {"center": v(45, -165) * mm, "radius": 0.5 * mm});
            skCircle(sketch, "E5.16.0.7", {"center": v(85, -165) * mm, "radius": 0.5 * mm});
            skCircle(sketch, "E5.16.0.8", {"center": v(95, -165) * mm, "radius": 0.5 * mm});
            skCircle(sketch, "E5.16.0.9", {"center": v(75, -165) * mm, "radius": 0.5 * mm});
            skCircle(sketch, "E5.16.0.10", {"center": v(55, -165) * mm, "radius": 0.5 * mm});
            skCircle(sketch, "E5.16.0.11", {"center": v(25, -165) * mm, "radius": 0.5 * mm});
            skCircle(sketch, "E5.16.0.12", {"center": v(35, -165) * mm, "radius": 0.5 * mm});
            skCircle(sketch, "E5.16.0.13", {"center": v(15, -165) * mm, "radius": 0.5 * mm});
            skCircle(sketch, "E5.16.0.14", {"center": v(5, -165) * mm, "radius": 0.5 * mm});
            skCircle(sketch, "E5.16.0.15", {"center": v(175, -165) * mm, "radius": 0.5 * mm});
            skCircle(sketch, "E5.16.0.16", {"center": v(155, -165) * mm, "radius": 0.5 * mm});
            skCircle(sketch, "E5.16.0.17", {"center": v(145, -165) * mm, "radius": 0.5 * mm});
            skCircle(sketch, "E5.16.0.18", {"center": v(165, -165) * mm, "radius": 0.5 * mm});
            skLineSegment(sketch, "E5.17.0.0", {"start": v(5, -175) * mm, "end": v(15, -175) * mm, "construction": true});
            skCircle(sketch, "E5.17.0.1", {"center": v(125, -175) * mm, "radius": 0.5 * mm});
            skCircle(sketch, "E5.17.0.2", {"center": v(115, -175) * mm, "radius": 0.5 * mm});
            skCircle(sketch, "E5.17.0.3", {"center": v(105, -175) * mm, "radius": 0.5 * mm});
            skCircle(sketch, "E5.17.0.4", {"center": v(65, -175) * mm, "radius": 0.5 * mm});
            skCircle(sketch, "E5.17.0.5", {"center": v(135, -175) * mm, "radius": 0.5 * mm});
            skCircle(sketch, "E5.17.0.6", {"center": v(45, -175) * mm, "radius": 0.5 * mm});
            skCircle(sketch, "E5.17.0.7", {"center": v(85, -175) * mm, "radius": 0.5 * mm});
            skCircle(sketch, "E5.17.0.8", {"center": v(95, -175) * mm, "radius": 0.5 * mm});
            skCircle(sketch, "E5.17.0.9", {"center": v(75, -175) * mm, "radius": 0.5 * mm});
            skCircle(sketch, "E5.17.0.10", {"center": v(55, -175) * mm, "radius": 0.5 * mm});
            skCircle(sketch, "E5.17.0.11", {"center": v(25, -175) * mm, "radius": 0.5 * mm});
            skCircle(sketch, "E5.17.0.12", {"center": v(35, -175) * mm, "radius": 0.5 * mm});
            skCircle(sketch, "E5.17.0.13", {"center": v(15, -175) * mm, "radius": 0.5 * mm});
            skCircle(sketch, "E5.17.0.14", {"center": v(5, -175) * mm, "radius": 0.5 * mm});
            skCircle(sketch, "E5.17.0.15", {"center": v(175, -175) * mm, "radius": 0.5 * mm});
            skCircle(sketch, "E5.17.0.16", {"center": v(155, -175) * mm, "radius": 0.5 * mm});
            skCircle(sketch, "E5.17.0.17", {"center": v(145, -175) * mm, "radius": 0.5 * mm});
            skCircle(sketch, "E5.17.0.18", {"center": v(165, -175) * mm, "radius": 0.5 * mm});
            skLineSegment(sketch, "E5.direction1", {"start": v(5, -5) * mm, "end": v(5, -15) * mm, "construction": true});
            skSolve(sketch);
        }
        {
            var Q0;
            Q0=makeQuery(id+"F0.imprint","IMPRINT",FACE,{"disambiguationData":[TD([[makeQuery(id+"F0.imprint","IMPRINT",EDGE,{"derivedFrom":sQuery(id+"F0.wireOp",EDGE,"E1.bottom")}),-1.0]])]});
            var Q1;
            Q1=makeQuery(id+"F0.imprint","IMPRINT",FACE,{"disambiguationData":[TD([[makeQuery(id+"F0.imprint","IMPRINT",EDGE,{"derivedFrom":sQuery(id+"F0.wireOp",EDGE,"E0.bottom")}),-1.0]])]});
            extrude(context, id + "F1", {"entities" : qUnion([Q0, Q1]), "depth" : 1.2 * mm, "offsetDistance" : 25 * mm});
        }
        {
            var Q0;
            Q0=makeQuery(id+"F0.imprint","IMPRINT",FACE,{"disambiguationData":[TD([[makeQuery(id+"F0.imprint","IMPRINT",EDGE,{"derivedFrom":sQuery(id+"F0.wireOp",EDGE,"E0.bottom")}),-1.0]])]});
            extrude(context, id + "F2", {"entities" : qUnion([Q0]), "operationType" : NewBodyOperationType.ADD, "depth" : 25 * mm, "offsetDistance" : 25 * mm});
        }
    });
